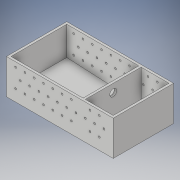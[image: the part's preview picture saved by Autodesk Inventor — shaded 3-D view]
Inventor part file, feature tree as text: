
AUTODESK INVENTOR PART (.ipt)
format: ipt  version: 2019 (Build 230136000, 136)  size: 243,712 bytes
history: native  units: mm
features: sketch x8, extrude x6, hole x2
ambient origin geometry x8: Origin, YZ Plane, XZ Plane, XY Plane, X Axis, Y Axis, Z Axis, Center Point
bodies: Solid1 (feature_tree)
feature tree (16):
  extrude  "Extrusion1"  Depth=230.0mm
  extrude  "Extrusion2"  Depth=5.0mm
  extrude  "Extrusion3"  Depth=5.0mm
  extrude  "Extrusion4"  Depth=70.0mm TaperAngle=0.0deg
  extrude  "Extrusion5"  Depth=60.0mm
  extrude  "Extrusion6"  Depth=70.0mm
  hole  "Hole2"  [1 undecoded]
  hole  "Hole3"  [1 undecoded]
  sketch  "Sketch1"  dims[d0=130.0mm d1=230.0mm]
  sketch  "Sketch2"  dims[d2=5.0mm d3=0.0mm d4=5.0mm]
  sketch  "Sketch3"  dims[d6=5.0mm d7=5.0mm]
  sketch  "Sketch4"  dims[d8=5.0mm d9=70.0mm d10=0.0mm]
  sketch  "Sketch6"  dims[d11=5.0mm d12=60.0mm]
  sketch  "Sketch7"  dims[d13=70.0mm d14=0.0mm d15=15.0mm]
  sketch  "Sketch8"  dims[d16=17.5mm d17=70.0mm d18=0.0mm]
  sketch  "Sketch9"  dims[d38=0.872665mm d39=0.523599mm d40=70.0mm d41=0.0mm d42=3.0mm d43=3.0mm d44=70.0mm d45=0.0mm d46=15.0mm d47=20.0mm d48=4.0mm d49=6.0mm d50=4.0mm d51=2.0mm d52=90.0deg d53=7.5mm d54=0.0mm d55=20.0mm d56=20.0mm d57=10.0mm d58=20.0mm d59=10.0mm d60=100.0mm d62=20.0mm d63=10.0mm d65=10.0mm d67=4.0mm d68=6.0mm d69=4.0mm d70=2.0mm d71=90.0deg d72=7.5mm d73=0.0mm]
note: 2 required parameter values undecoded (feature->parameter linkage not recoverable at this tier; creation-order binding heuristic only, values carry confidence <= 0.55)
